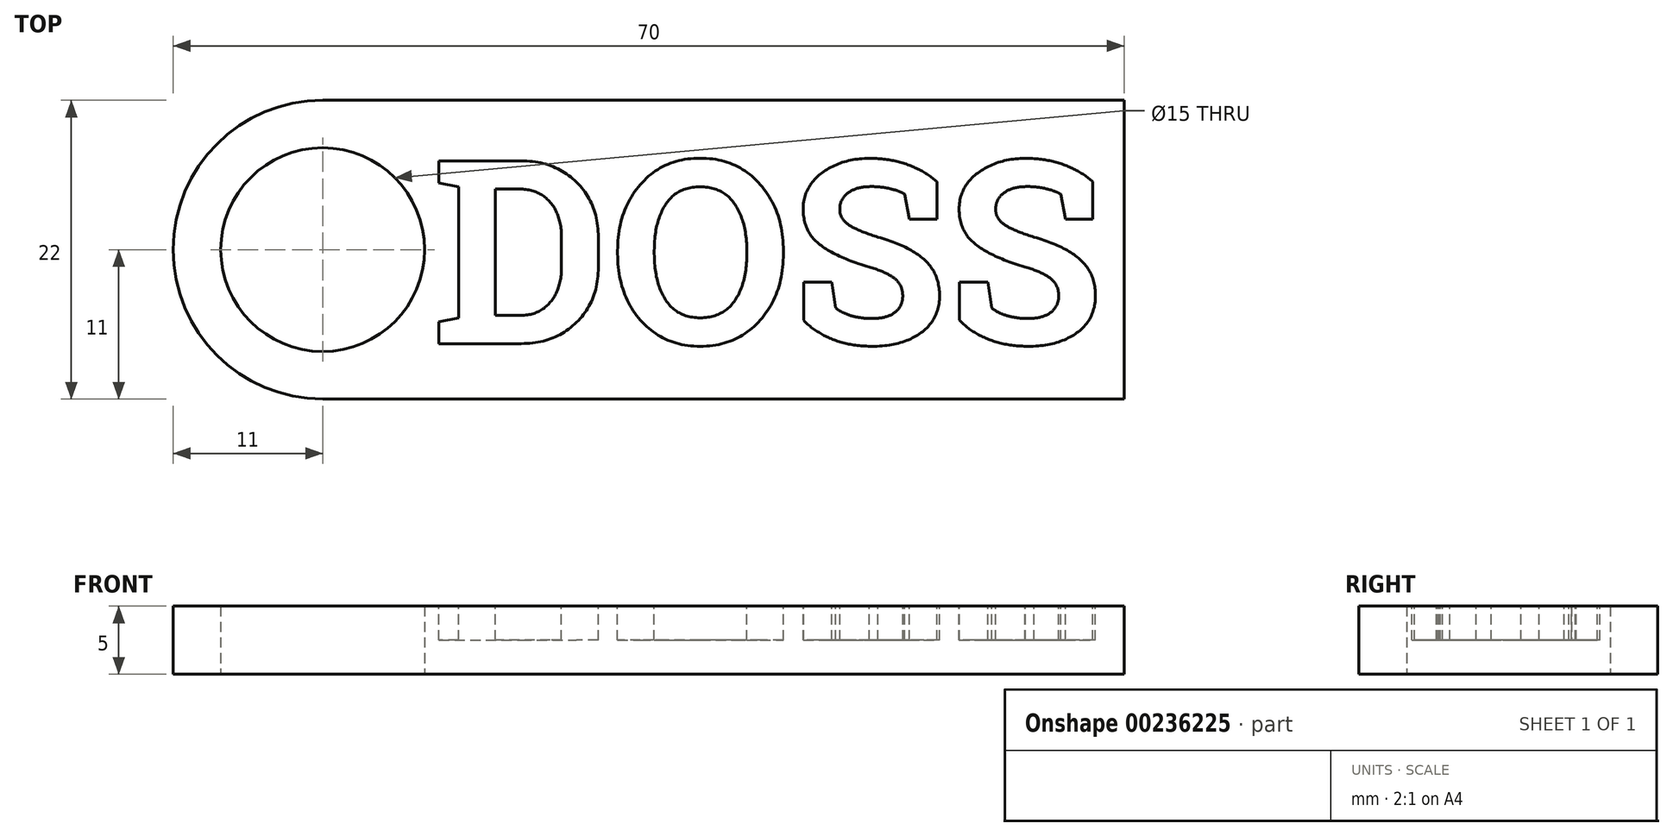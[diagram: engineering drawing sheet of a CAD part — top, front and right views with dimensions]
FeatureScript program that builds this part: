
annotation { "Feature Type Name" : "Feature", "Feature Type Description" : "" }
export const myFeature = defineFeature(function(context is Context, id is Id, definition is map)
    precondition{}
    {
        {
            var Q0;
            Q0=qCreatedBy(makeId("Top.planeOp"),FACE);
            var sketch = newSketch(context, id + "F0", { "sketchPlane" : qUnion([Q0])});
            skLineSegment(sketch, "E0", {"start": v(11, 0) * mm, "end": v(70, 0) * mm});
            skLineSegment(sketch, "E1", {"start": v(70, 0) * mm, "end": v(70, -22) * mm});
            skLineSegment(sketch, "E2", {"start": v(11, -22) * mm, "end": v(70, -22) * mm});
            skPoint(sketch, "E3", {"position": v(11, 0) * mm});
            skPoint(sketch, "E4", {"position": v(11, -22) * mm});
            skPoint(sketch, "E5", {"position": v(0, -11) * mm});
            skArc(sketch, "E6", {"start": v(11, 0) * mm, "mid": v(0, -11) * mm, "end": v(11, -22) * mm});
            skPoint(sketch, "E7.orphan", {"position": v(0, -22) * mm});
            skPoint(sketch, "E8.start.orphan", {"position": v(0, 0) * mm});
            skCircle(sketch, "E9", {"center": v(11, -11) * mm, "radius": 7.5 * mm});
            skSolve(sketch);
        }
        {
            var Q0;
            Q0 = qSketchRegion(id + "F0", true);
            extrude(context, id + "F1", {"entities" : qUnion([Q0]), "depth" : 5 * mm});
        }
        {
            var Q0;
            Q0=makeQuery(id+"F1.opExtrude","CAP_FACE",FACE,{"disambiguationData":[OSD([sQuery(id+"F0.wireOp",EDGE,"E0"),sQuery(id+"F0.wireOp",EDGE,"E1"),sQuery(id+"F0.wireOp",EDGE,"E2"),sQuery(id+"F0.wireOp",EDGE,"E6"),sQuery(id+"F0.wireOp",EDGE,"E9")])],"isStart":false});
            var sketch = newSketch(context, id + "F2", { "sketchPlane" : qUnion([Q0])});
            skText(sketch, "E10", { "text": "DOSS", "fontName": "RobotoSlab-Bold.ttf"});
            const initialGuessF2  = {"E10": [0.01905, -0.01792, 1, 0, 0.01363]};
            skSetInitialGuess(sketch, initialGuessF2);
            skSolve(sketch);
        }
        {
            var Q0;
            Q0 = qSketchRegion(id + "F2", true);
            extrude(context, id + "F3", {"entities" : qUnion([Q0]), "operationType" : NewBodyOperationType.REMOVE, "oppositeDirection" : true, "depth" : 2.5 * mm});
        }
    });
